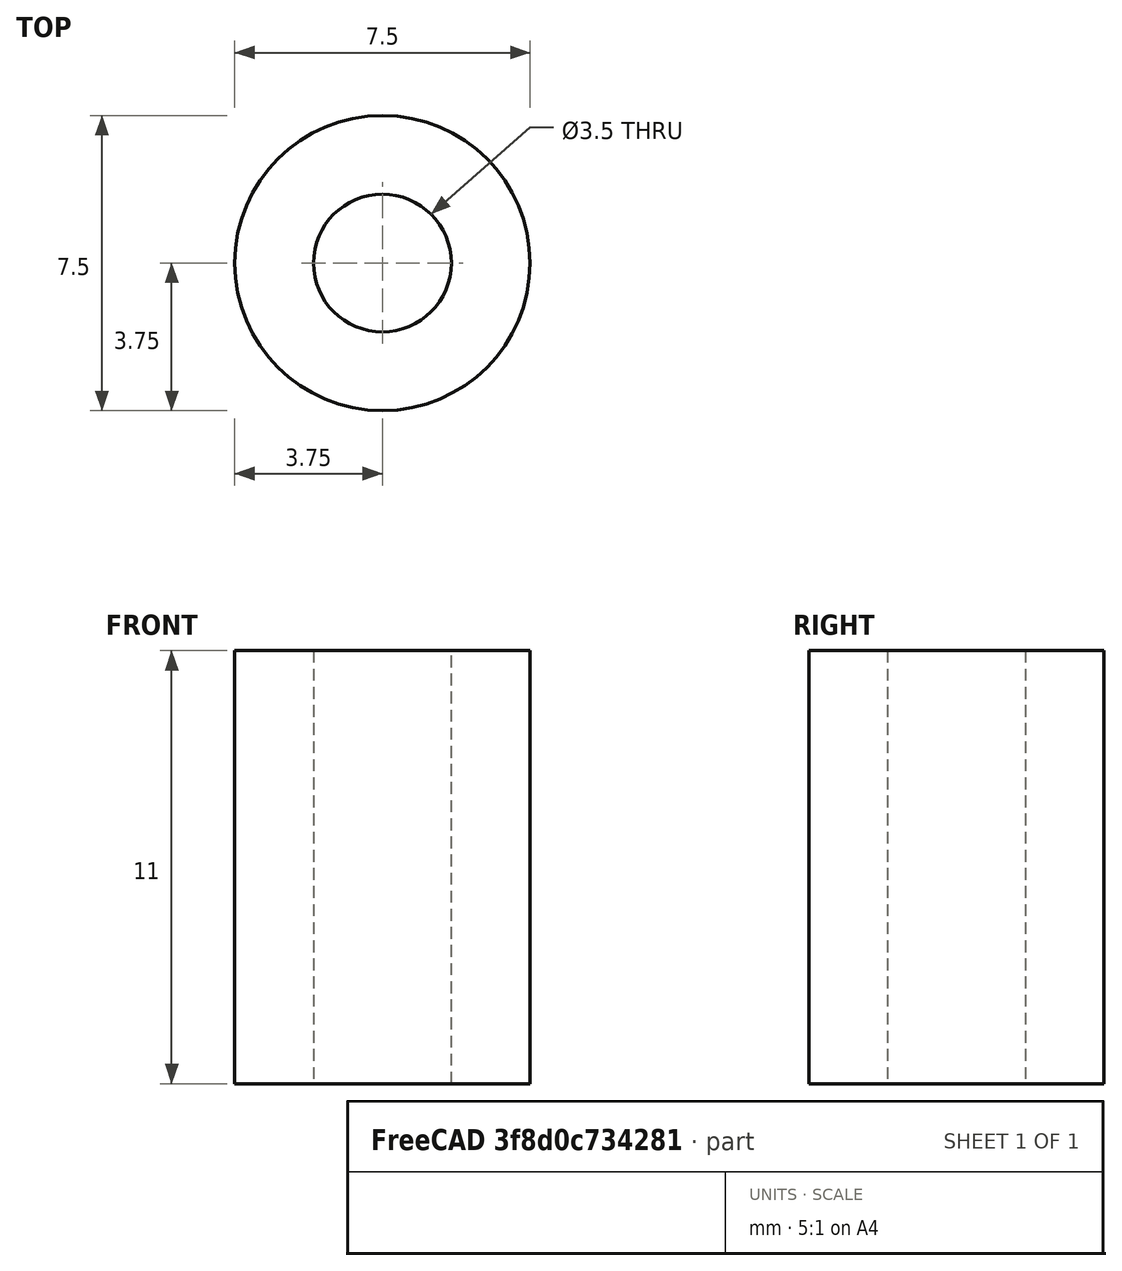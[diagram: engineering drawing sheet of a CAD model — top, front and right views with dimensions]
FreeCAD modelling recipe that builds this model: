
FCSTD DOCUMENT  (FreeCAD 0.21R33668 +26 (Git))
Label: KM5GT_Switch_Matrix_Spacer_V12
License: All rights reserved
LicenseURL: http://en.wikipedia.org/wiki/All_rights_reserved
objects: Sketcher::SketchObject×1, PartDesign::Pad×1, PartDesign::Body×1
note: 4 computed .brp shape members not serialized (recipe doc carries the construction recipe); baked Part::Feature solids carry a one-line shape summary decoded from their .brp

FEATURE [Sketcher::SketchObject] Sketch  label="spacer"
  FullyConstrained = true
  MapMode = 5
  Support = -> [XY_Plane]
  sketch-geometry (2):
    g0: Circle CenterX=0 CenterY=0 CenterZ=0 NormalX=0 NormalY=0 NormalZ=1 AngleXU=0 Radius=1.75
    g1: Circle CenterX=0 CenterY=0 CenterZ=0 NormalX=0 NormalY=0 NormalZ=1 AngleXU=0 Radius=3.75
  constraints (4):
    c: Coincident(g0,g-1)
    c: Coincident(g1,g0)
    c: Diameter(g0) = 3.5
    c: Distance(g0,g1) = 2
FEATURE [PartDesign::Pad] Pad  label="spacerPad"
  Direction = (0,0,1)
  Length = 11
  Length2 = 10
  Profile = -> Sketch
  ReferenceAxis = -> Sketch [N_Axis]
  Type = 0
FEATURE [PartDesign::Body] Body
  Group = -> [Sketch,Pad]
  Origin = -> Origin
  Tip = -> Pad
